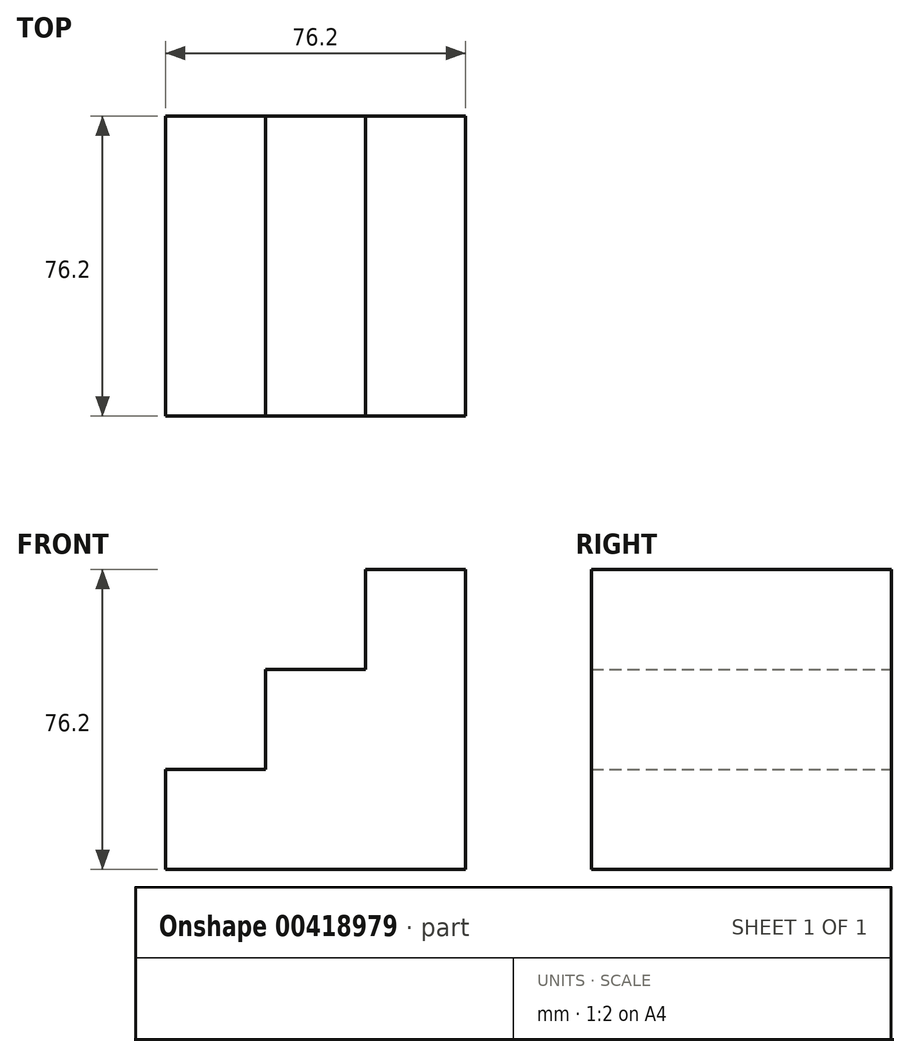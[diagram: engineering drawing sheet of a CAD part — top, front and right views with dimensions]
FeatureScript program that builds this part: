
annotation { "Feature Type Name" : "Feature", "Feature Type Description" : "" }
export const myFeature = defineFeature(function(context is Context, id is Id, definition is map)
    precondition{}
    {
        {
            var Q0;
            Q0=qCreatedBy(makeId("Front.planeOp"),FACE);
            var sketch = newSketch(context, id + "F0", { "sketchPlane" : qUnion([Q0])});
            skLineSegment(sketch, "E0", {"start": v(-76.2, 0) * mm, "end": v(0, 0) * mm});
            skLineSegment(sketch, "E1", {"start": v(0, 0) * mm, "end": v(0, 76.2) * mm});
            skLineSegment(sketch, "E2", {"start": v(0, 76.2) * mm, "end": v(-25.4, 76.2) * mm});
            skLineSegment(sketch, "E3", {"start": v(-25.4, 76.2) * mm, "end": v(-25.4, 50.8) * mm});
            skLineSegment(sketch, "E4", {"start": v(-25.4, 50.8) * mm, "end": v(-50.8, 50.8) * mm});
            skLineSegment(sketch, "E5", {"start": v(-50.8, 50.8) * mm, "end": v(-50.8, 25.4) * mm});
            skLineSegment(sketch, "E6", {"start": v(-50.8, 25.4) * mm, "end": v(-76.2, 25.4) * mm});
            skLineSegment(sketch, "E7", {"start": v(-76.2, 25.4) * mm, "end": v(-76.2, 0) * mm});
            skSolve(sketch);
        }
        {
            var Q0;
            Q0=makeQuery(id+"F0.imprint","IMPRINT",FACE,{"disambiguationData":[TD([[makeQuery(id+"F0.imprint","IMPRINT",EDGE,{"derivedFrom":sQuery(id+"F0.wireOp",EDGE,"E0")}),1.0]])]});
            extrude(context, id + "F1", {"entities" : qUnion([Q0]), "depth" : 76.2 * mm});
        }
    });
